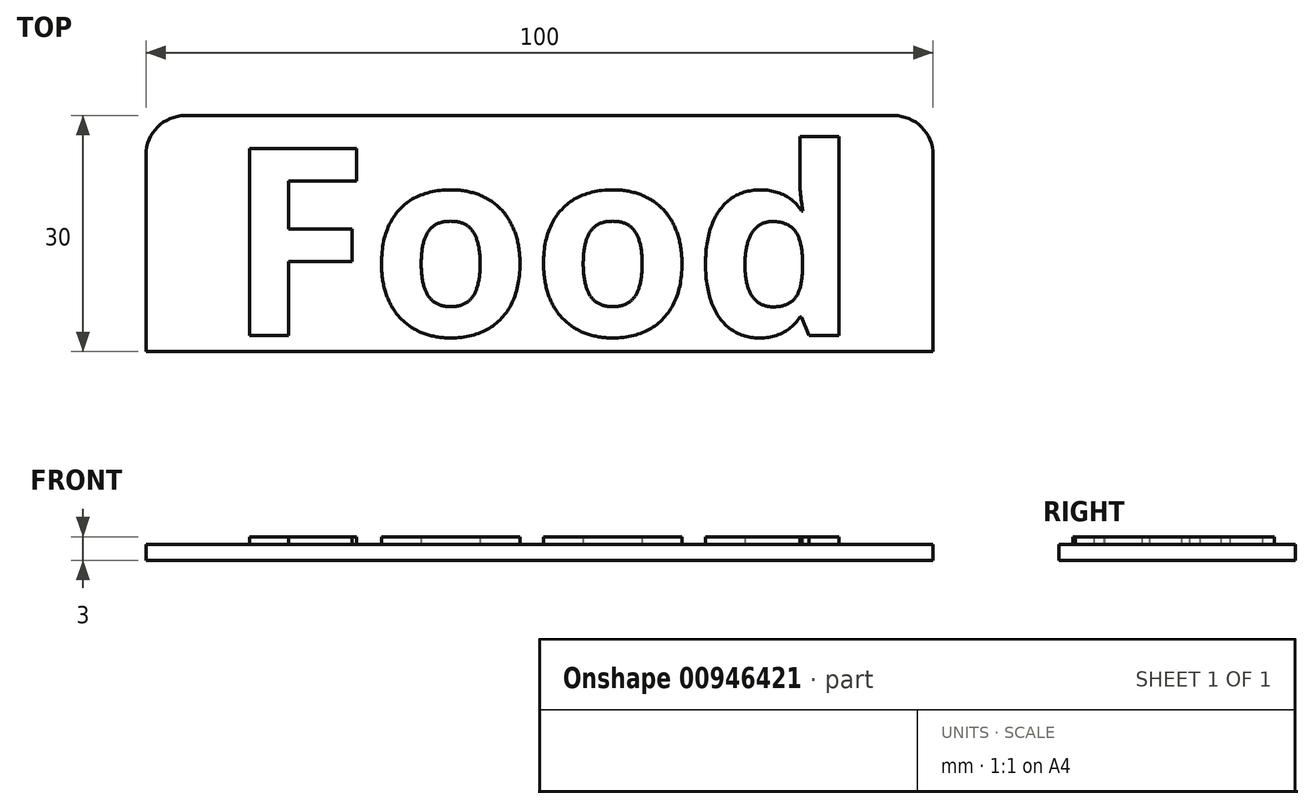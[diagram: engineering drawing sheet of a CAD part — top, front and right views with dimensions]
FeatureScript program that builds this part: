
annotation { "Feature Type Name" : "Feature", "Feature Type Description" : "" }
export const myFeature = defineFeature(function(context is Context, id is Id, definition is map)
    precondition{}
    {
        {
            var Q0;
            Q0=qCreatedBy(makeId("Top.planeOp"),FACE);
            var sketch = newSketch(context, id + "F0", { "sketchPlane" : qUnion([Q0])});
            skLineSegment(sketch, "E0.bottom", {"start": v(-50, 15) * mm, "end": v(50, 15) * mm});
            skLineSegment(sketch, "E0.top", {"start": v(-50, -15) * mm, "end": v(50, -15) * mm});
            skLineSegment(sketch, "E0.left", {"start": v(-50, 15) * mm, "end": v(-50, -15) * mm});
            skLineSegment(sketch, "E0.right", {"start": v(50, 15) * mm, "end": v(50, -15) * mm});
            skPoint(sketch, "E0.middle", {"position": v(0, 0) * mm});
            skSolve(sketch);
        }
        {
            var Q0;
            Q0 = qSketchRegion(id + "F0", true);
            extrude(context, id + "F1", {"entities" : qUnion([Q0]), "depth" : 2 * mm, "offsetDistance" : 25 * mm});
        }
        {
            var Q0;
            Q0=makeQuery(id+"F1.opExtrude","CAP_FACE",FACE,{"disambiguationData":[OSD([sQuery(id+"F0.wireOp",EDGE,"E0.bottom"),sQuery(id+"F0.wireOp",EDGE,"E0.top"),sQuery(id+"F0.wireOp",EDGE,"E0.left"),sQuery(id+"F0.wireOp",EDGE,"E0.right")])],"isStart":false});
            var sketch = newSketch(context, id + "F2", { "sketchPlane" : qUnion([Q0])});
            skText(sketch, "E1", { "text": "Food\n", "fontName": "NotoSans-Bold.ttf"});
            const initialGuessF2  = {"E1": [-0.03981, -0.01292, 1, 0, 0.02393]};
            skSetInitialGuess(sketch, initialGuessF2);
            skSolve(sketch);
        }
        {
            var Q0;
            Q0 = qSketchRegion(id + "F2", true);
            extrude(context, id + "F3", {"entities" : qUnion([Q0]), "operationType" : NewBodyOperationType.ADD, "depth" : 1 * mm, "offsetDistance" : 25 * mm});
        }
        {
            var Q0;
            Q0=makeQuery(id+"F1.opExtrude","SWEPT_EDGE",EDGE,{"disambiguationData":[OSD([sQuery(id+"F0.wireOp",EDGE,"E0.bottom"),sQuery(id+"F0.wireOp",EDGE,"E0.left")])]});
            var Q1;
            Q1=makeQuery(id+"F1.opExtrude","SWEPT_EDGE",EDGE,{"disambiguationData":[OSD([sQuery(id+"F0.wireOp",EDGE,"E0.bottom"),sQuery(id+"F0.wireOp",EDGE,"E0.right")])]});
            fillet(context, id + "F4", {"entities" : qUnion([Q0, Q1]), "radius" : 5 * mm, "tangentPropagation" : true, "allowEdgeOverflow" : false});
        }
    });
